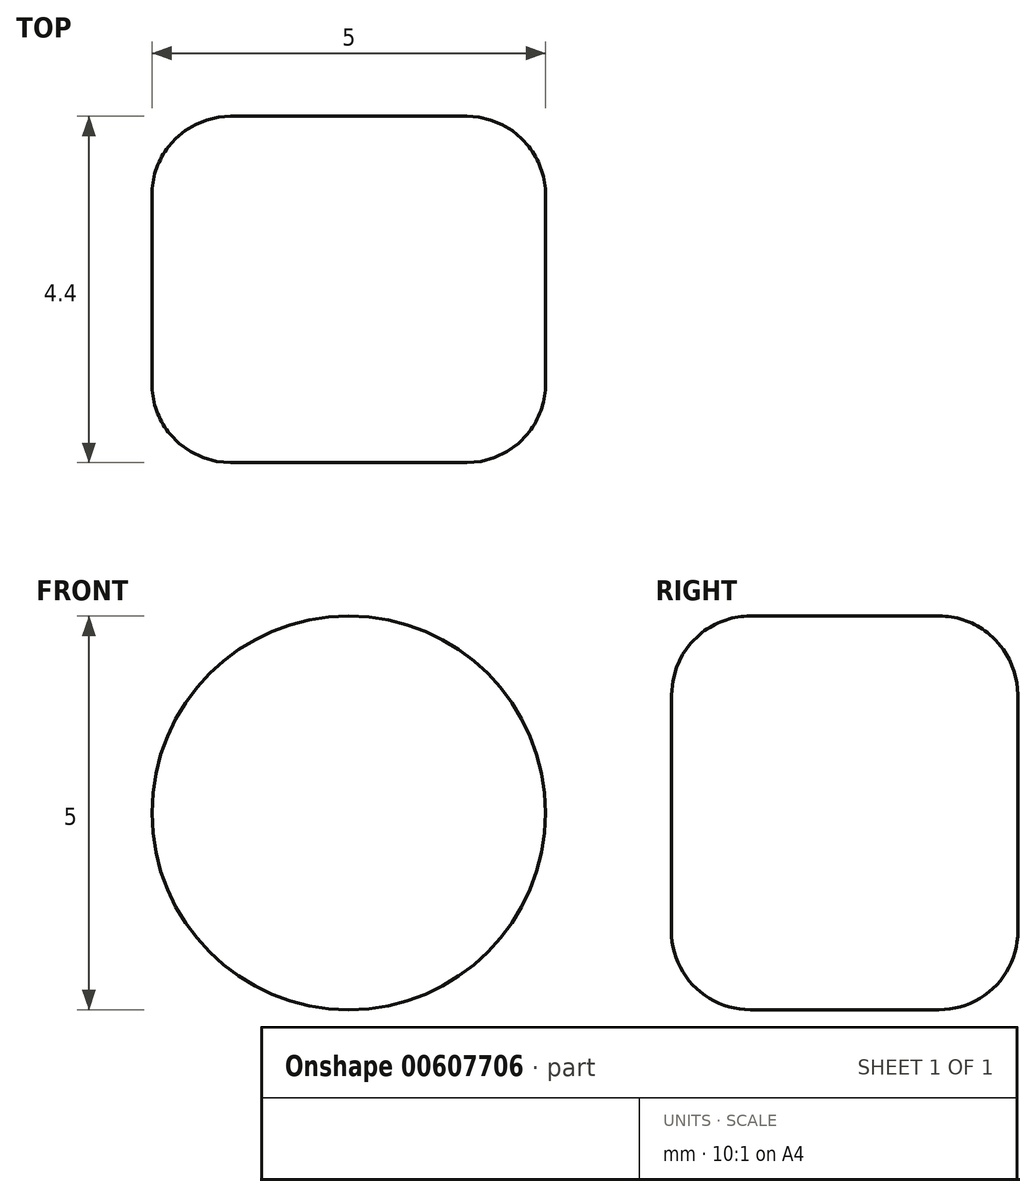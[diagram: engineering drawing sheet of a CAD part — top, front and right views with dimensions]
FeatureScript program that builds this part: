
annotation { "Feature Type Name" : "Feature", "Feature Type Description" : "" }
export const myFeature = defineFeature(function(context is Context, id is Id, definition is map)
    precondition{}
    {
        {
            var Q0;
            Q0=qCreatedBy(makeId("Front.planeOp"),FACE);
            var sketch = newSketch(context, id + "F0", { "sketchPlane" : qUnion([Q0])});
            skCircle(sketch, "E0", {"center": v(0, 0) * mm, "radius": 2.5 * mm});
            skSolve(sketch);
        }
        {
            var Q0;
            Q0=qSketchRegion(id+"F0",true);
            extrude(context, id + "F1", {"entities" : qUnion([Q0]), "depth" : 4.4 * mm, "offsetDistance" : 25 * mm});
        }
        {
            var Q0;
            Q0=makeQuery(id+"F1.opExtrude","CAP_EDGE",EDGE,{"disambiguationData":[OSD([sQuery(id+"F0.wireOp",EDGE,"E0")])],"isStart":false});
            var Q1;
            Q1=makeQuery(id+"F1.opExtrude","CAP_EDGE",EDGE,{"disambiguationData":[OSD([sQuery(id+"F0.wireOp",EDGE,"E0")])],"isStart":true});
            fillet(context, id + "F2", {"entities" : qUnion([Q0, Q1]), "radius" : 1 * mm, "tangentPropagation" : true, "allowEdgeOverflow" : false});
        }
    });
